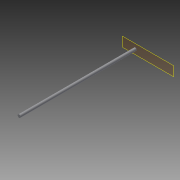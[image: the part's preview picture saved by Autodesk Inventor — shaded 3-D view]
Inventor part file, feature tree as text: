
AUTODESK INVENTOR PART (.ipt)
format: ipt  version: 2015 (Build 190159000, 159)  size: 68,608 bytes
history: native  units: in
note: dims shown in document units (in); Inventor stores cm internally (conversion verified against a paired STEP export)
features: reference x2, plane x1, extrude x1, sketch x1
ambient origin geometry x8: Origin, YZ Plane, XZ Plane, XY Plane, X Axis, Y Axis, Z Axis, Center Point
bodies: Solid1 (feature_tree)
feature tree (5):
  plane  "Work Plane1"
  extrude  "Extrusion1"  [1 undecoded]
  sketch  "Sketch1"  dims[d2=10.0in d3=0.0in]
  reference  "Reference1"
  reference  "Reference2"
note: 1 required parameter value undecoded (feature->parameter linkage not recoverable at this tier; creation-order binding heuristic only, values carry confidence <= 0.55)
